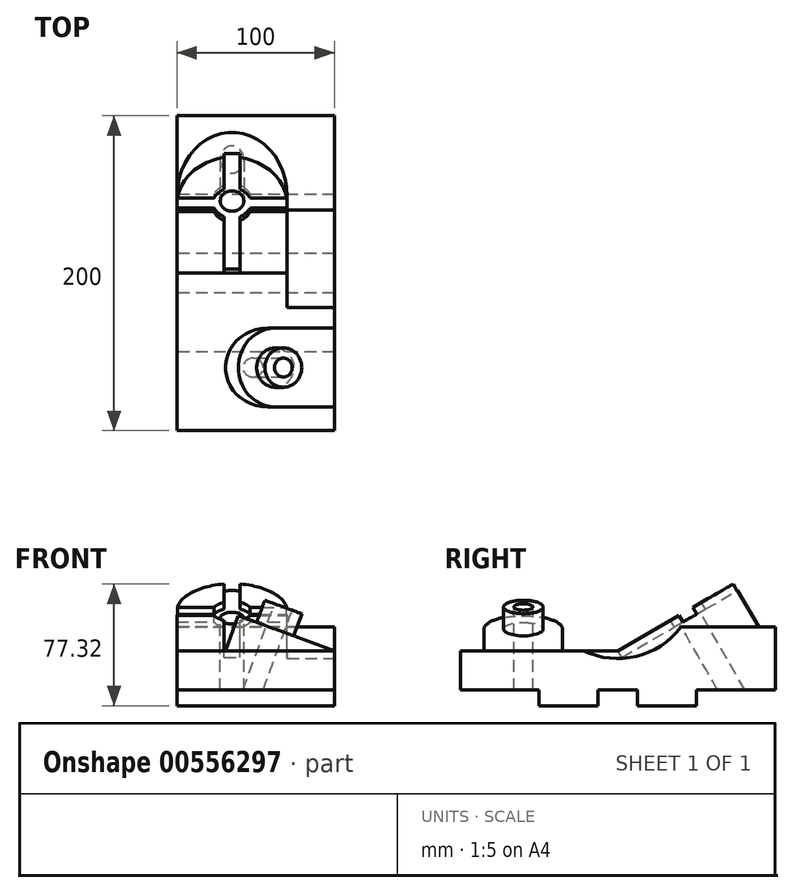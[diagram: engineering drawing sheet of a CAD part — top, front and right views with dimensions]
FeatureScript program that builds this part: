
annotation { "Feature Type Name" : "Feature", "Feature Type Description" : "" }
export const myFeature = defineFeature(function(context is Context, id is Id, definition is map)
    precondition{}
    {
        {
            var Q0;
            Q0=qCreatedBy(makeId("Right.planeOp"),FACE);
            var sketch = newSketch(context, id + "F0", { "sketchPlane" : qUnion([Q0])});
            skLineSegment(sketch, "E0", {"start": v(-144.5, -10.42) * mm, "end": v(-144.5, -35.42) * mm});
            skLineSegment(sketch, "E1", {"start": v(-144.5, -35.42) * mm, "end": v(-94.5, -35.42) * mm});
            skLineSegment(sketch, "E2", {"start": v(-94.5, -35.42) * mm, "end": v(-94.5, -45.42) * mm});
            skLineSegment(sketch, "E3", {"start": v(-94.5, -45.42) * mm, "end": v(-57, -45.42) * mm});
            skLineSegment(sketch, "E4", {"start": v(-57, -45.42) * mm, "end": v(-57, -35.42) * mm});
            skLineSegment(sketch, "E5", {"start": v(-57, -35.42) * mm, "end": v(-32, -35.42) * mm});
            skLineSegment(sketch, "E6", {"start": v(-32, -35.42) * mm, "end": v(-32, -45.42) * mm});
            skLineSegment(sketch, "E7", {"start": v(-32, -45.42) * mm, "end": v(5.5, -45.42) * mm});
            skLineSegment(sketch, "E8", {"start": v(5.5, -45.42) * mm, "end": v(5.5, -35.42) * mm});
            skLineSegment(sketch, "E9", {"start": v(5.5, -35.42) * mm, "end": v(55.5, -35.42) * mm});
            skLineSegment(sketch, "E10", {"start": v(55.5, -35.42) * mm, "end": v(55.5, 4.58) * mm});
            skLineSegment(sketch, "E11", {"start": v(55.5, 4.58) * mm, "end": v(-8.43, 4.58) * mm});
            skLineSegment(sketch, "E12", {"start": v(-8.43, 4.58) * mm, "end": v(-8.43, -10.42) * mm});
            skLineSegment(sketch, "E13", {"start": v(-8.43, -10.42) * mm, "end": v(-144.5, -10.42) * mm});
            skSolve(sketch);
        }
        {
            var Q0;
            Q0 = qSketchRegion(id + "F0", true);
            extrude(context, id + "F1", {"entities" : qUnion([Q0]), "depth" : 100 * mm, "offsetDistance" : 25 * mm});
        }
        {
            var Q0;
            Q0=makeQuery(id+"F1.opExtrude","CAP_EDGE",EDGE,{"disambiguationData":[OSD([sQuery(id+"F0.wireOp",EDGE,"E13")])],"isStart":false});
            cPlane(context, id + "F2", {"entities" : qUnion([Q0]), "cplaneType" : CPlaneType.LINE_ANGLE, "offset" : 25 * mm, "angle" : 20 * degree, "oppositeDirection" : true, "width" : 150 * mm, "height" : 150 * mm});
        }
        {
            var Q0;
            Q0=qCreatedBy(id+"F2.planeOp",FACE);
            var sketch = newSketch(context, id + "F3", { "sketchPlane" : qUnion([Q0])});
            skLineSegment(sketch, "E14.bottom", {"start": v(97.53, 129.5) * mm, "end": v(57.53, 129.5) * mm});
            skLineSegment(sketch, "E14.top", {"start": v(97.53, 79.5) * mm, "end": v(57.53, 79.5) * mm});
            skLineSegment(sketch, "E14.left", {"start": v(97.53, 129.5) * mm, "end": v(97.53, 79.5) * mm});
            skArc(sketch, "E15", {"start": v(57.53, 129.5) * mm, "mid": v(32.53, 104.5) * mm, "end": v(57.53, 79.5) * mm});
            skSolve(sketch);
        }
        {
            var Q0;
            Q0 = qSketchRegion(id + "F3", true);
            extrude(context, id + "F4", {"entities" : qUnion([Q0]), "operationType" : NewBodyOperationType.ADD, "depth" : 25 * mm, "offsetDistance" : 25 * mm});
        }
        {
            var Q0;
            Q0=makeQuery(id+"F4.opExtrude","CAP_FACE",FACE,{"disambiguationData":[OSD([sQuery(id+"F3.wireOp",EDGE,"E14.bottom"),sQuery(id+"F3.wireOp",EDGE,"E14.top"),sQuery(id+"F3.wireOp",EDGE,"E14.left"),sQuery(id+"F3.wireOp",EDGE,"E15")])],"isStart":true});
            var sketch = newSketch(context, id + "F5", { "sketchPlane" : qUnion([Q0])});
            skCircle(sketch, "E16", {"center": v(57.53, -104.5) * mm, "radius": 12.5 * mm});
            skSolve(sketch);
        }
        {
            var Q0;
            Q0 = qSketchRegion(id + "F5", true);
            extrude(context, id + "F6", {"entities" : qUnion([Q0]), "operationType" : NewBodyOperationType.ADD, "depth" : 15 * mm, "offsetDistance" : 25 * mm});
        }
        {
            var Q0;
            Q0=makeQuery(id+"F6.opExtrude","CAP_FACE",FACE,{"disambiguationData":[OSD([sQuery(id+"F5.wireOp",EDGE,"E16")])],"isStart":false});
            var sketch = newSketch(context, id + "F7", { "sketchPlane" : qUnion([Q0])});
            skCircle(sketch, "E17", {"center": v(57.53, -104.5) * mm, "radius": 6 * mm});
            skSolve(sketch);
        }
        {
            var Q0;
            Q0 = qSketchRegion(id + "F7", true);
            extrude(context, id + "F8", {"entities" : qUnion([Q0]), "operationType" : NewBodyOperationType.REMOVE, "endBound" : BoundingType.THROUGH_ALL, "oppositeDirection" : true, "depth" : 25 * mm, "offsetDistance" : 25 * mm});
        }
        {
            var Q0;
            Q0=makeQuery(id+"F1.opExtrude","SWEPT_FACE",FACE,{"disambiguationData":[OSD([sQuery(id+"F0.wireOp",EDGE,"E13")])]});
            var sketch = newSketch(context, id + "F9", { "sketchPlane" : qUnion([Q0])});
            skLineSegment(sketch, "E18", {"start": v(0, -44.5) * mm, "end": v(100, -44.5) * mm});
            skSolve(sketch);
        }
        {
            var Q0;
            Q0=sQuery(id+"F9.wireOp",EDGE,"E18");
            var Q1;
            {var subQ1=sQuery(id+"F0.wireOp",EDGE,"E13");var subQ2=sQuery(id+"F0.wireOp",EDGE,"E12");Q1=makeQuery(id+"F4.boolean.opBoolean","SPLIT",EDGE,{"disambiguationData":[TD([makeQuery(id+"F1.opExtrude","SWEPT_FACE",FACE,{"disambiguationData":[OSD([subQ2])]})])],"derivedFrom":makeQuery(id+"F1.opExtrude","CAP_EDGE",EDGE,{"disambiguationData":[OSD([subQ1])],"isStart":false})});}
            cPlane(context, id + "F10", {"entities" : qUnion([Q0, Q1]), "cplaneType" : CPlaneType.LINE_ANGLE, "offset" : 25 * mm, "angle" : 30 * degree, "width" : 150 * mm, "height" : 150 * mm});
        }
        {
            var Q0;
            Q0=qCreatedBy(id+"F10.planeOp",FACE);
            var sketch = newSketch(context, id + "F11", { "sketchPlane" : qUnion([Q0])});
            skLineSegment(sketch, "E19.bottom", {"start": v(0, 43.75) * mm, "end": v(70, 43.75) * mm});
            skLineSegment(sketch, "E19.left", {"start": v(0, 43.75) * mm, "end": v(0, -6.25) * mm});
            skLineSegment(sketch, "E19.right", {"start": v(70, 43.75) * mm, "end": v(70, -6.25) * mm});
            skArc(sketch, "E20", {"start": v(0, -6.25) * mm, "mid": v(35, -41.25) * mm, "end": v(70, -6.25) * mm});
            skSolve(sketch);
        }
        {
            var Q0;
            Q0 = qSketchRegion(id + "F11", true);
            var Q1;
            Q1 = qSketchRegion(id + "F9", true);
            extrude(context, id + "F12", {"entities" : qUnion([Q0, Q1]), "operationType" : NewBodyOperationType.ADD, "depth" : 35 * mm, "offsetDistance" : 25 * mm});
        }
        {
            var Q0;
            Q0=makeQuery(id+"F12.opExtrude","CAP_FACE",FACE,{"disambiguationData":[OSD([sQuery(id+"F11.wireOp",EDGE,"E19.bottom"),sQuery(id+"F11.wireOp",EDGE,"E19.left"),sQuery(id+"F11.wireOp",EDGE,"E19.right"),sQuery(id+"F11.wireOp",EDGE,"E20")])],"isStart":true});
            var sketch = newSketch(context, id + "F13", { "sketchPlane" : qUnion([Q0])});
            skLineSegment(sketch, "E21.0", {"start": v(0, 1.25) * mm, "end": v(23.54, 1.25) * mm});
            skLineSegment(sketch, "E22.0", {"start": v(0, 11.25) * mm, "end": v(23.54, 11.25) * mm});
            skLineSegment(sketch, "E23.0", {"start": v(40, -43.75) * mm, "end": v(40, -5.2) * mm});
            skLineSegment(sketch, "E24.0", {"start": v(30, -43.75) * mm, "end": v(30, -5.2) * mm});
            skPoint(sketch, "E25.orphan", {"position": v(35, -43.75) * mm});
            skLineSegment(sketch, "E26.trimOffspring", {"start": v(46.46, 1.25) * mm, "end": v(69.64, 1.25) * mm});
            skLineSegment(sketch, "E27.trimOffspring", {"start": v(40, 17.7) * mm, "end": v(40, 40.9) * mm});
            skLineSegment(sketch, "E28.trimOffspring", {"start": v(46.46, 11.25) * mm, "end": v(69.64, 11.25) * mm});
            skLineSegment(sketch, "E29.trimOffspring", {"start": v(30, 17.7) * mm, "end": v(30, 40.9) * mm});
            skArc(sketch, "E30", {"start": v(69.64, 11.25) * mm, "mid": v(35, 41.25) * mm, "end": v(0.36, 11.25) * mm});
            skArc(sketch, "E31", {"start": v(40, -5.2) * mm, "mid": v(43.84, -2.59) * mm, "end": v(46.46, 1.25) * mm});
            skArc(sketch, "E32.trimOffspring", {"start": v(23.54, 1.25) * mm, "mid": v(26.16, -2.59) * mm, "end": v(30, -5.2) * mm});
            skArc(sketch, "E33.trimOffspring", {"start": v(30, 17.7) * mm, "mid": v(26.16, 15.1) * mm, "end": v(23.54, 11.25) * mm});
            skArc(sketch, "E34.trimOffspring", {"start": v(46.46, 11.25) * mm, "mid": v(43.84, 15.1) * mm, "end": v(40, 17.7) * mm});
            skLineSegment(sketch, "E35.bottom", {"start": v(69.64, 1.25) * mm, "end": v(83.76, 1.25) * mm});
            skLineSegment(sketch, "E35.top", {"start": v(69.64, 11.25) * mm, "end": v(83.76, 11.25) * mm});
            skLineSegment(sketch, "E35.right", {"start": v(83.76, 1.25) * mm, "end": v(83.76, 11.25) * mm});
            skSolve(sketch);
        }
        {
            var Q0;
            {var subQ8=sQuery(id+"F13.wireOp",EDGE,"E21.0");Q0=makeQuery(id+"F13.imprint","IMPRINT",FACE,{"disambiguationData":[TD([[makeQuery(id+"F13.imprint","IMPRINT",EDGE,{"derivedFrom":subQ8}),1.0]])]});}
            extrude(context, id + "F14", {"entities" : qUnion([Q0]), "operationType" : NewBodyOperationType.REMOVE, "oppositeDirection" : true, "depth" : 5 * mm, "offsetDistance" : 25 * mm});
        }
        {
            var Q0;
            Q0=makeQuery(id+"F14.boolean.opBoolean","COPY",FACE,{"derivedFrom":makeQuery(id+"F14.opExtrude","CAP_FACE",FACE,{"disambiguationData":[OSD([sQuery(id+"F11.wireOp",EDGE,"E19.bottom"),sQuery(id+"F11.wireOp",EDGE,"E19.left"),sQuery(id+"F11.wireOp",EDGE,"E19.right"),sQuery(id+"F11.wireOp",EDGE,"E20"),sQuery(id+"F13.wireOp",EDGE,"E21.0"),sQuery(id+"F13.wireOp",EDGE,"E22.0"),sQuery(id+"F13.wireOp",EDGE,"E23.0"),sQuery(id+"F13.wireOp",EDGE,"E24.0"),sQuery(id+"F13.wireOp",EDGE,"E26.trimOffspring"),sQuery(id+"F13.wireOp",EDGE,"E27.trimOffspring"),sQuery(id+"F13.wireOp",EDGE,"E28.trimOffspring"),sQuery(id+"F13.wireOp",EDGE,"E29.trimOffspring"),sQuery(id+"F13.wireOp",EDGE,"E30"),sQuery(id+"F13.wireOp",EDGE,"E31"),sQuery(id+"F13.wireOp",EDGE,"E32.trimOffspring"),sQuery(id+"F13.wireOp",EDGE,"E33.trimOffspring"),sQuery(id+"F13.wireOp",EDGE,"E34.trimOffspring"),sQuery(id+"F13.wireOp",EDGE,"E35.bottom")])],"isStart":false})});
            var sketch = newSketch(context, id + "F15", { "sketchPlane" : qUnion([Q0])});
            skCircle(sketch, "E36", {"center": v(35, 6.25) * mm, "radius": 7.5 * mm});
            skSolve(sketch);
        }
        {
            var Q0;
            Q0=makeQuery(id+"F15.imprint","IMPRINT",FACE,{"disambiguationData":[TD([[makeQuery(id+"F15.imprint","IMPRINT",EDGE,{"derivedFrom":sQuery(id+"F15.wireOp",EDGE,"E36")}),1.0]])]});
            extrude(context, id + "F16", {"entities" : qUnion([Q0]), "operationType" : NewBodyOperationType.REMOVE, "endBound" : BoundingType.THROUGH_ALL, "oppositeDirection" : true, "depth" : 25 * mm, "offsetDistance" : 25 * mm});
        }
        {
            var Q0;
            {var subQ0=sQuery(id+"F9.wireOp",EDGE,"E18");Q0=makeQuery(id+"F9.imprint","IMPRINT",FACE,{"disambiguationData":[TD([[makeQuery(id+"F9.imprint","IMPRINT",EDGE,{"derivedFrom":subQ0}),1.0]])]});}
            var sketch = newSketch(context, id + "F17", { "sketchPlane" : qUnion([Q0])});
            skLineSegment(sketch, "E37.bottom", {"start": v(100, -44.5) * mm, "end": v(70, -44.5) * mm});
            skLineSegment(sketch, "E37.top", {"start": v(100, -8.43) * mm, "end": v(70, -8.43) * mm});
            skLineSegment(sketch, "E37.left", {"start": v(100, -44.5) * mm, "end": v(100, -8.43) * mm});
            skLineSegment(sketch, "E37.right", {"start": v(70, -44.5) * mm, "end": v(70, -8.43) * mm});
            skSolve(sketch);
        }
        {
            var Q0;
            Q0 = qSketchRegion(id + "F17", true);
            var Q1;
            Q1=makeQuery(id+"F1.opExtrude","SWEPT_FACE",FACE,{"disambiguationData":[OSD([sQuery(id+"F0.wireOp",EDGE,"E11")])]});
            extrude(context, id + "F18", {"entities" : qUnion([Q0]), "operationType" : NewBodyOperationType.ADD, "endBound" : BoundingType.UP_TO_SURFACE, "depth" : 25 * mm, "endBoundEntityFace" : qUnion([Q1]), "offsetDistance" : 25 * mm});
        }
        {
            var Q0;
            Q0=makeQuery(id+"F18.boolean.opBoolean","MERGE",FACE,{"derivedFrom":[makeQuery(id+"F1.opExtrude","CAP_FACE",FACE,{"disambiguationData":[OSD([sQuery(id+"F0.wireOp",EDGE,"E0"),sQuery(id+"F0.wireOp",EDGE,"E1"),sQuery(id+"F0.wireOp",EDGE,"E2"),sQuery(id+"F0.wireOp",EDGE,"E3"),sQuery(id+"F0.wireOp",EDGE,"E4"),sQuery(id+"F0.wireOp",EDGE,"E5"),sQuery(id+"F0.wireOp",EDGE,"E6"),sQuery(id+"F0.wireOp",EDGE,"E7"),sQuery(id+"F0.wireOp",EDGE,"E8"),sQuery(id+"F0.wireOp",EDGE,"E9"),sQuery(id+"F0.wireOp",EDGE,"E10"),sQuery(id+"F0.wireOp",EDGE,"E11"),sQuery(id+"F0.wireOp",EDGE,"E12"),sQuery(id+"F0.wireOp",EDGE,"E13")])],"isStart":false}),makeQuery(id+"F18.opExtrude","SWEPT_FACE",FACE,{"disambiguationData":[OSD([sQuery(id+"F17.wireOp",EDGE,"E37.left")])]})]});
            var sketch = newSketch(context, id + "F19", { "sketchPlane" : qUnion([Q0])});
            skLineSegment(sketch, "E38", {"start": v(-69.98, -15.42) * mm, "end": v(6.85, -15.42) * mm, "construction": true});
            skArc(sketch, "E39", {"start": v(-74.25, -5.6) * mm, "mid": v(4.04, 22.59) * mm, "end": v(-52.1, 84) * mm});
            skLineSegment(sketch, "E40", {"start": v(-4.5, 4.58) * mm, "end": v(55.5, 4.58) * mm, "construction": true});
            skLineSegment(sketch, "E41", {"start": v(-52.1, 84) * mm, "end": v(-74.25, -5.6) * mm});
            skSolve(sketch);
        }
        {
            var Q0;
            {var subQ0=sQuery(id+"F19.wireOp",EDGE,"E41");Q0=makeQuery(id+"F19.imprint","IMPRINT",FACE,{"disambiguationData":[TD([[makeQuery(id+"F19.imprint","IMPRINT",EDGE,{"derivedFrom":subQ0}),1.0]])]});}
            var Q1;
            {var subQ7=sQuery(id+"F17.wireOp",EDGE,"E37.left");var subQ10=makeQuery(id+"F18.opExtrude","SWEPT_EDGE",EDGE,{"disambiguationData":[OSD([sQuery(id+"F17.wireOp",EDGE,"E37.bottom"),subQ7])]});Q1=makeQuery(id+"F19.imprint","IMPRINT",FACE,{"disambiguationData":[TD([[makeQuery(id+"F19.imprint","IMPRINT",EDGE,{"derivedFrom":subQ10}),1.0]])]});}
            var Q2;
            Q2=makeQuery(id+"F12.opExtrude","SWEPT_FACE",FACE,{"disambiguationData":[OSD([sQuery(id+"F11.wireOp",EDGE,"E19.right")])]});
            extrude(context, id + "F20", {"entities" : qUnion([Q0, Q1]), "operationType" : NewBodyOperationType.REMOVE, "endBound" : BoundingType.UP_TO_SURFACE, "oppositeDirection" : true, "depth" : 30 * mm, "endBoundEntityFace" : qUnion([Q2]), "offsetDistance" : 25 * mm});
        }
    });
